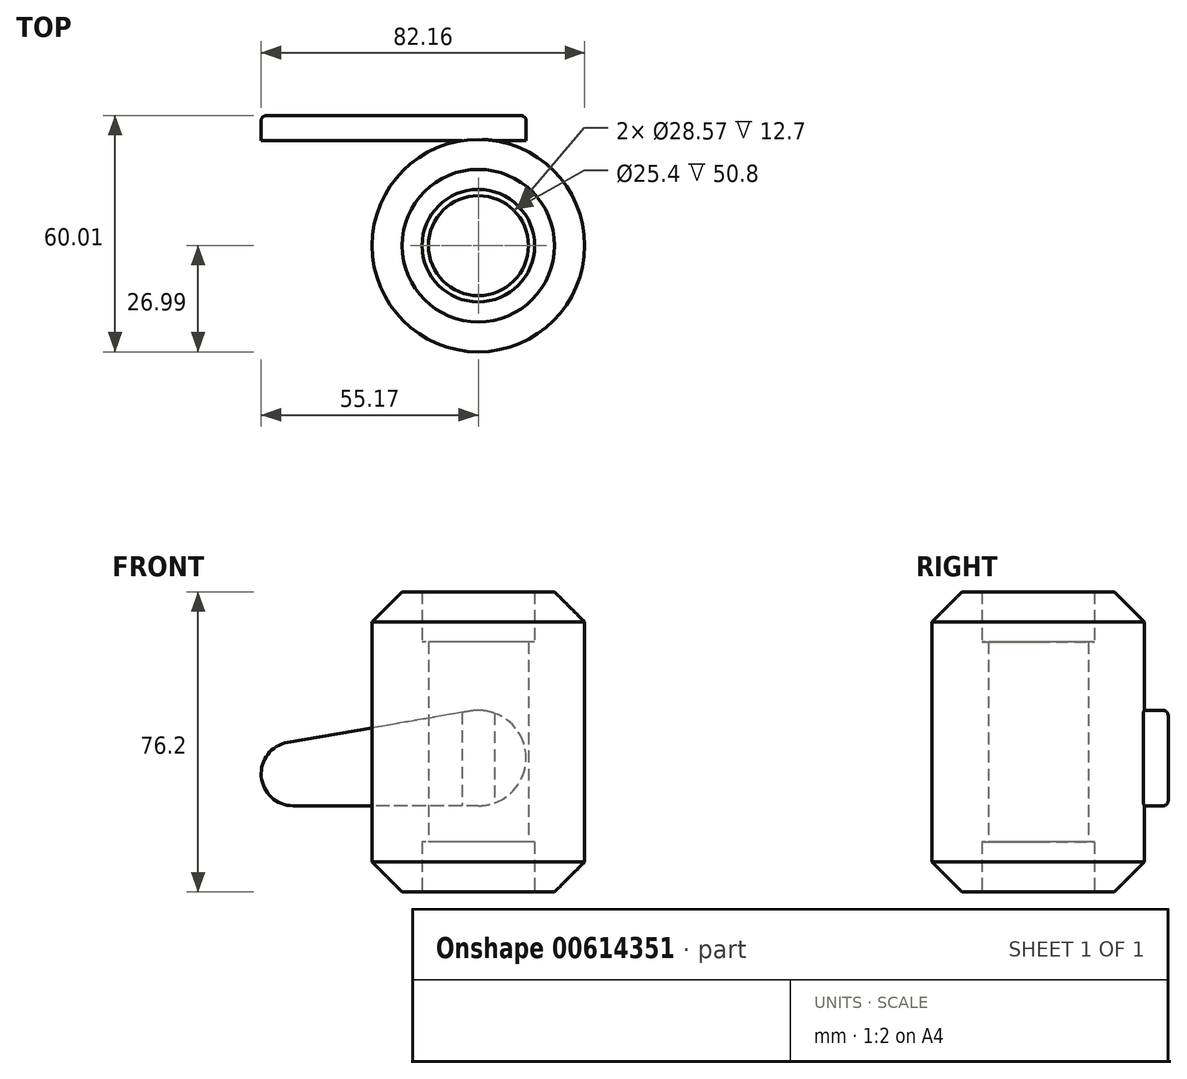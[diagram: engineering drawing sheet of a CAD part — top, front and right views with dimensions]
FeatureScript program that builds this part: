
annotation { "Feature Type Name" : "Feature", "Feature Type Description" : "" }
export const myFeature = defineFeature(function(context is Context, id is Id, definition is map)
    precondition{}
    {
        {
            var Q0;
            Q0=qCreatedBy(makeId("Top.planeOp"),FACE);
            var sketch = newSketch(context, id + "F0", { "sketchPlane" : qUnion([Q0])});
            skLineSegment(sketch, "E0", {"start": v(0, 0) * mm, "end": v(12.7, 0) * mm});
            skCircle(sketch, "E1", {"center": v(0, 0) * mm, "radius": 12.7 * mm});
            skCircle(sketch, "E2.0", {"center": v(0, 0) * mm, "radius": 14.29 * mm});
            skSolve(sketch);
        }
        {
            var Q0;
            Q0=qCreatedBy(makeId("Top.planeOp"),FACE);
            var sketch = newSketch(context, id + "F1", { "sketchPlane" : qUnion([Q0])});
            skSolve(sketch);
        }
        {
            var Q0;
            Q0=qSketchRegion(id+"F1",true);
            var Q1;
            Q1=makeQuery(id+"F0.imprint","IMPRINT",FACE,{"disambiguationData":[TD([[makeQuery(id+"F0.imprint","IMPRINT",EDGE,{"derivedFrom":sQuery(id+"F0.wireOp",EDGE,"E1")}),-1.0]])]});
            extrude(context, id + "F2", {"entities" : qUnion([Q0, Q1]), "depth" : 50.8 * mm, "offsetDistance" : 25.4 * mm});
        }
        {
            var Q0;
            Q0=qSketchRegion(id+"F0",true);
            var sketch = newSketch(context, id + "F3", { "sketchPlane" : qUnion([Q0])});
            skCircle(sketch, "E3.0", {"center": v(0, 0) * mm, "radius": 26.99 * mm});
            skSolve(sketch);
        }
        {
            var Q0;
            Q0=makeQuery(id+"F3.imprint","IMPRINT",FACE,{"disambiguationData":[TD([[makeQuery(id+"F3.imprint","IMPRINT",EDGE,{"derivedFrom":sQuery(id+"F3.wireOp",EDGE,"E3.0")}),1.0]])]});
            var Q1;
            Q1=sQuery(id+"F0.wireOp",EDGE,"E2.0");
            var Q2;
            Q2=sQuery(id+"F3.wireOp",EDGE,"E3.0");
            extrude(context, id + "F4", {"entities" : qUnion([Q0]), "operationType" : NewBodyOperationType.ADD, "surfaceEntities" : qUnion([Q1, Q2]), "depth" : 63.5 * mm, "offsetDistance" : 25.4 * mm, "hasSecondDirection" : true, "secondDirectionOppositeDirection" : true, "secondDirectionDepth" : 12.7 * mm});
        }
        {
            var Q0;
            Q0=makeQuery(id+"F4.opExtrude","CAP_EDGE",EDGE,{"disambiguationData":[OSD([sQuery(id+"F3.wireOp",EDGE,"E3.0")])],"isStart":false});
            var Q1;
            Q1=makeQuery(id+"F4.opExtrude","CAP_EDGE",EDGE,{"disambiguationData":[OSD([sQuery(id+"F3.wireOp",EDGE,"E3.0")])],"isStart":true});
            chamfer(context, id + "F5", {"entities" : qUnion([Q0, Q1]), "width" : 7.62 * mm, "tangentPropagation" : true});
        }
        {
            var Q0;
            Q0=qCreatedBy(makeId("Front.planeOp"),FACE);
            var sketch = newSketch(context, id + "F6", { "sketchPlane" : qUnion([Q0])});
            skCircle(sketch, "E4", {"center": v(0, 21.29) * mm, "radius": 12.12 * mm});
            skCircle(sketch, "E5", {"center": v(-47.06, 17.28) * mm, "radius": 8.1 * mm});
            skLineSegment(sketch, "E6", {"start": v(-2.05, 33.23) * mm, "end": v(-48.43, 25.27) * mm});
            skLineSegment(sketch, "E7", {"start": v(0, 9.17) * mm, "end": v(-47.06, 9.17) * mm});
            skSolve(sketch);
        }
        {
            var Q0;
            Q0=qSketchRegion(id+"F6",true);
            extrude(context, id + "F7", {"entities" : qUnion([Q0]), "operationType" : NewBodyOperationType.ADD, "oppositeDirection" : true, "depth" : 33.02 * mm, "offsetDistance" : 25.4 * mm, "hasSecondDirection" : true, "secondDirectionOppositeDirection" : true, "secondDirectionDepth" : 26.67 * mm});
        }
        {
            var Q0;
            Q0=makeQuery(id+"F7.opExtrude","CAP_FACE",FACE,{"disambiguationData":[OSD([sQuery(id+"F6.wireOp",EDGE,"E4"),sQuery(id+"F6.wireOp",EDGE,"E5"),sQuery(id+"F6.wireOp",EDGE,"E6"),sQuery(id+"F6.wireOp",EDGE,"E7")])],"isStart":false});
            fillet(context, id + "F8", {"entities" : qUnion([Q0]), "radius" : 1.27 * mm, "tangentPropagation" : true, "allowEdgeOverflow" : false});
        }
    });
